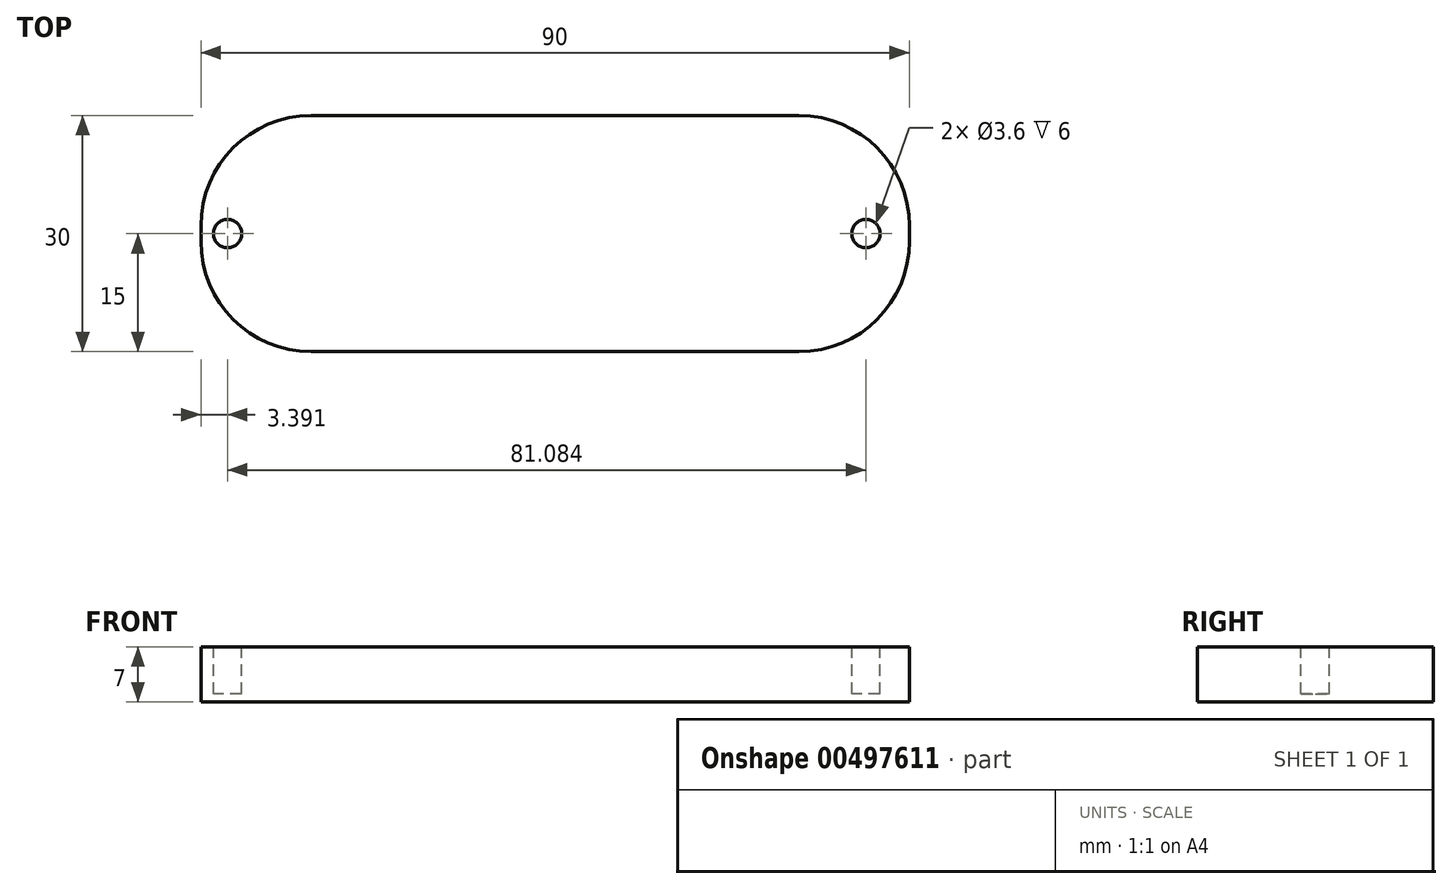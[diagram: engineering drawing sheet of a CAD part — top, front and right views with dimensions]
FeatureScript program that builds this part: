
annotation { "Feature Type Name" : "Feature", "Feature Type Description" : "" }
export const myFeature = defineFeature(function(context is Context, id is Id, definition is map)
    precondition{}
    {
        {
            var Q0;
            Q0=qCreatedBy(makeId("Top.planeOp"),FACE);
            var sketch = newSketch(context, id + "F0", { "sketchPlane" : qUnion([Q0])});
            skLineSegment(sketch, "E0.bottom", {"start": v(31, 15) * mm, "end": v(-31, 15) * mm});
            skLineSegment(sketch, "E0.top", {"start": v(31, -15) * mm, "end": v(-31, -15) * mm});
            skLineSegment(sketch, "E0.left", {"start": v(45, 1) * mm, "end": v(45, -1) * mm});
            skLineSegment(sketch, "E0.right", {"start": v(-45, 1) * mm, "end": v(-45, -1) * mm});
            skPoint(sketch, "E0.middle", {"position": v(0, 0) * mm});
            skPoint(sketch, "E1.visualSharp", {"position": v(-45, 15) * mm});
            skArc(sketch, "E1.filletArc", {"start": v(-31, 15) * mm, "mid": v(-40.9, 10.9) * mm, "end": v(-45, 1) * mm});
            skPoint(sketch, "E2.visualSharp", {"position": v(-45, -15) * mm});
            skArc(sketch, "E2.filletArc", {"start": v(-45, -1) * mm, "mid": v(-40.9, -10.9) * mm, "end": v(-31, -15) * mm});
            skPoint(sketch, "E3.visualSharp", {"position": v(45, -15) * mm});
            skArc(sketch, "E3.filletArc", {"start": v(31, -15) * mm, "mid": v(40.9, -10.9) * mm, "end": v(45, -1) * mm});
            skPoint(sketch, "E4.visualSharp", {"position": v(45, 15) * mm});
            skArc(sketch, "E4.filletArc", {"start": v(45, 1) * mm, "mid": v(40.9, 10.9) * mm, "end": v(31, 15) * mm});
            skSolve(sketch);
        }
        {
            var Q0;
            Q0 = qSketchRegion(id + "F0", true);
            extrude(context, id + "F1", {"entities" : qUnion([Q0]), "endBound" : BoundingType.SYMMETRIC, "depth" : 7 * mm});
        }
        {
            var Q0;
            Q0=makeQuery(id+"F1.opExtrude","CAP_FACE",FACE,{"disambiguationData":[OSD([sQuery(id+"F0.wireOp",EDGE,"E0.bottom"),sQuery(id+"F0.wireOp",EDGE,"E0.top"),sQuery(id+"F0.wireOp",EDGE,"E0.left"),sQuery(id+"F0.wireOp",EDGE,"E0.right"),sQuery(id+"F0.wireOp",EDGE,"E1.filletArc"),sQuery(id+"F0.wireOp",EDGE,"E2.filletArc"),sQuery(id+"F0.wireOp",EDGE,"E3.filletArc"),sQuery(id+"F0.wireOp",EDGE,"E4.filletArc")])],"isStart":false});
            var sketch = newSketch(context, id + "F2", { "sketchPlane" : qUnion([Q0])});
            skCircle(sketch, "E5", {"center": v(39.47, 0) * mm, "radius": 1.8 * mm});
            skSolve(sketch);
        }
        {
            var Q0;
            Q0 = qSketchRegion(id + "F2", true);
            extrude(context, id + "F3", {"entities" : qUnion([Q0]), "operationType" : NewBodyOperationType.REMOVE, "oppositeDirection" : true, "depth" : 6 * mm});
        }
        {
            var Q0;
            Q0=makeQuery(id+"F1.opExtrude","CAP_FACE",FACE,{"disambiguationData":[OSD([sQuery(id+"F0.wireOp",EDGE,"E0.bottom"),sQuery(id+"F0.wireOp",EDGE,"E0.top"),sQuery(id+"F0.wireOp",EDGE,"E0.left"),sQuery(id+"F0.wireOp",EDGE,"E0.right"),sQuery(id+"F0.wireOp",EDGE,"E1.filletArc"),sQuery(id+"F0.wireOp",EDGE,"E2.filletArc"),sQuery(id+"F0.wireOp",EDGE,"E3.filletArc"),sQuery(id+"F0.wireOp",EDGE,"E4.filletArc")])],"isStart":false});
            var sketch = newSketch(context, id + "F4", { "sketchPlane" : qUnion([Q0])});
            skCircle(sketch, "E6", {"center": v(-41.6, 0) * mm, "radius": 1.8 * mm});
            skPoint(sketch, "E6.centerSnap0", {"position": v(-44.9, 0) * mm});
            skSolve(sketch);
        }
        {
            var Q0;
            Q0 = qSketchRegion(id + "F4", true);
            extrude(context, id + "F5", {"entities" : qUnion([Q0]), "operationType" : NewBodyOperationType.REMOVE, "oppositeDirection" : true, "depth" : 6 * mm});
        }
    });
